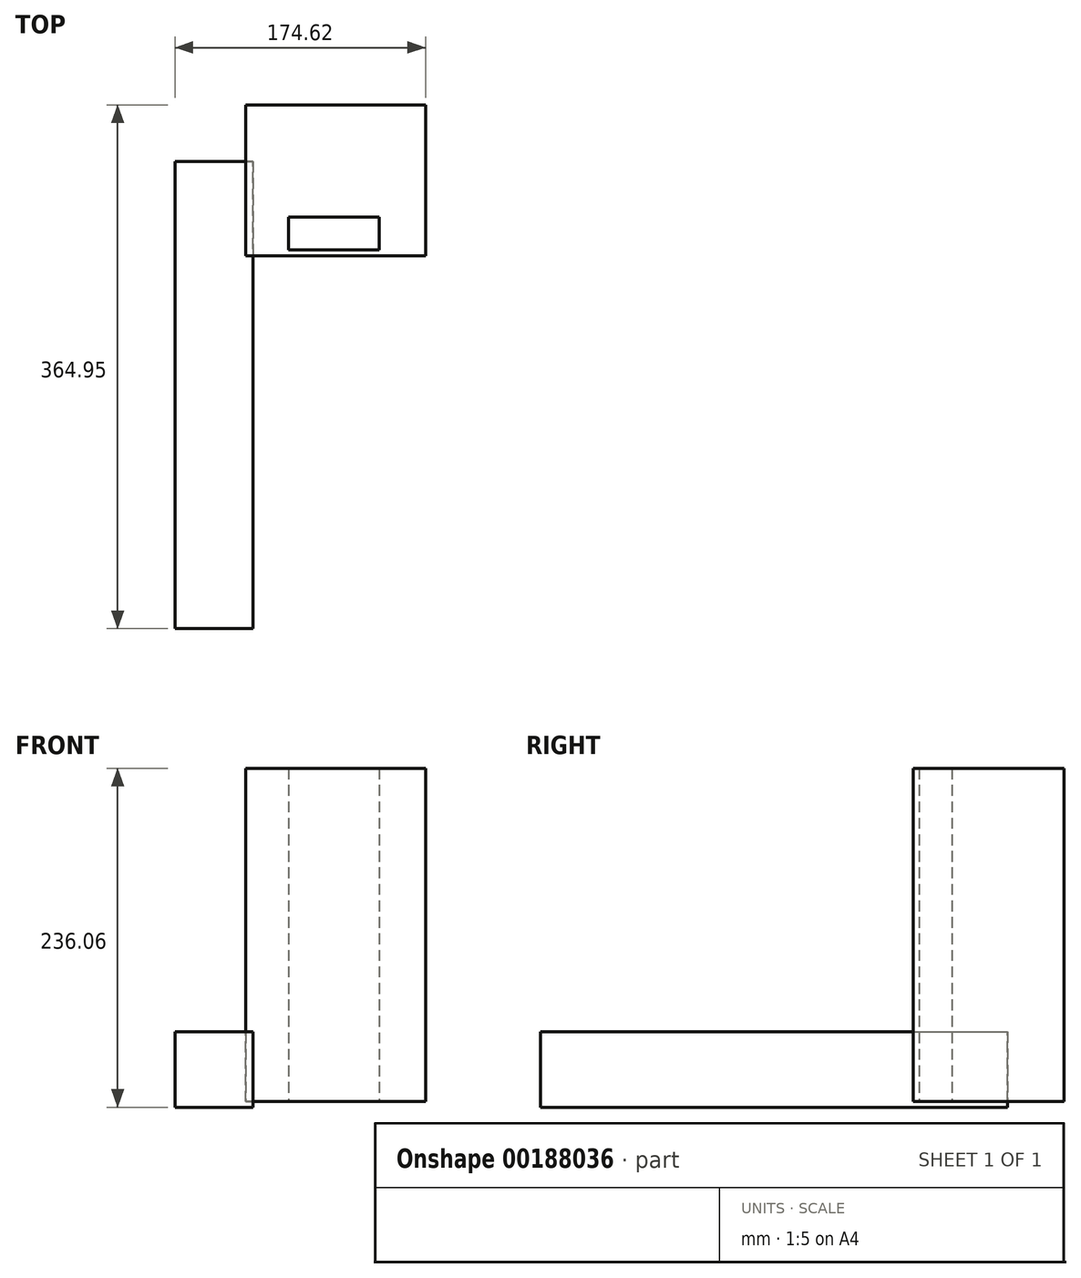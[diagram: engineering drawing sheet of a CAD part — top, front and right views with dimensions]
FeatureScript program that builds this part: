
annotation { "Feature Type Name" : "Feature", "Feature Type Description" : "" }
export const myFeature = defineFeature(function(context is Context, id is Id, definition is map)
    precondition{}
    {
        {
            var Q0;
            Q0=qCreatedBy(makeId("Front.planeOp"),FACE);
            var sketch = newSketch(context, id + "F0", { "sketchPlane" : qUnion([Q0])});
            skLineSegment(sketch, "E0.bottom", {"start": v(-122.13, 57.07) * mm, "end": v(-15.62, 57.07) * mm});
            skLineSegment(sketch, "E0.top", {"start": v(-122.13, -23.37) * mm, "end": v(-15.62, -23.37) * mm});
            skLineSegment(sketch, "E0.left", {"start": v(-122.13, 57.07) * mm, "end": v(-122.13, -23.37) * mm});
            skLineSegment(sketch, "E0.right", {"start": v(-15.62, 57.07) * mm, "end": v(-15.62, -23.37) * mm});
            skLineSegment(sketch, "E1.bottom", {"start": v(-109.51, 48.54) * mm, "end": v(-55.15, 48.54) * mm});
            skLineSegment(sketch, "E1.top", {"start": v(-109.51, -3.9) * mm, "end": v(-55.15, -3.9) * mm});
            skLineSegment(sketch, "E1.left", {"start": v(-109.51, 48.54) * mm, "end": v(-109.51, -3.9) * mm});
            skLineSegment(sketch, "E1.right", {"start": v(-55.15, 48.54) * mm, "end": v(-55.15, -3.9) * mm});
            skSolve(sketch);
        }
        {
            var Q0;
            Q0=qCreatedBy(makeId("Top.planeOp"),FACE);
            var sketch = newSketch(context, id + "F1", { "sketchPlane" : qUnion([Q0])});
            skLineSegment(sketch, "E2.bottom", {"start": v(-60.2, 39.58) * mm, "end": v(65.1, 39.58) * mm});
            skLineSegment(sketch, "E2.top", {"start": v(-60.2, -65.7) * mm, "end": v(65.1, -65.7) * mm});
            skLineSegment(sketch, "E2.left", {"start": v(-60.2, 39.58) * mm, "end": v(-60.2, -65.7) * mm});
            skLineSegment(sketch, "E2.right", {"start": v(65.1, 39.58) * mm, "end": v(65.1, -65.7) * mm});
            skCircle(sketch, "E3", {"center": v(0, 0) * mm, "radius": 36.13 * mm});
            skLineSegment(sketch, "E4.bottom", {"start": v(-30.25, -61.5) * mm, "end": v(32.88, -61.5) * mm});
            skLineSegment(sketch, "E4.top", {"start": v(-30.25, -38.62) * mm, "end": v(32.88, -38.62) * mm});
            skLineSegment(sketch, "E4.left", {"start": v(-30.25, -61.5) * mm, "end": v(-30.25, -38.62) * mm});
            skLineSegment(sketch, "E4.right", {"start": v(32.88, -61.5) * mm, "end": v(32.88, -38.62) * mm});
            skSolve(sketch);
        }
        {
            var Q0;
            Q0=makeQuery(id+"F0.imprint","IMPRINT",FACE,{"disambiguationData":[TD([[makeQuery(id+"F0.imprint","IMPRINT",EDGE,{"derivedFrom":sQuery(id+"F0.wireOp",EDGE,"E1.bottom")}),-1.0]])]});
            extrude(context, id + "F2", {"entities" : qUnion([Q0]), "depth" : 325.37 * mm});
        }
        {
            var Q0;
            Q0=makeQuery(id+"F1.imprint","IMPRINT",FACE,{"disambiguationData":[TD([[makeQuery(id+"F1.imprint","IMPRINT",EDGE,{"derivedFrom":sQuery(id+"F1.wireOp",EDGE,"E3")}),1.0]])]});
            var Q1;
            Q1=makeQuery(id+"F1.imprint","IMPRINT",FACE,{"disambiguationData":[TD([[makeQuery(id+"F1.imprint","IMPRINT",EDGE,{"derivedFrom":sQuery(id+"F1.wireOp",EDGE,"E2.bottom")}),-1.0]])]});
            extrude(context, id + "F3", {"entities" : qUnion([Q0, Q1]), "operationType" : NewBodyOperationType.ADD, "depth" : 232.16 * mm});
        }
    });
